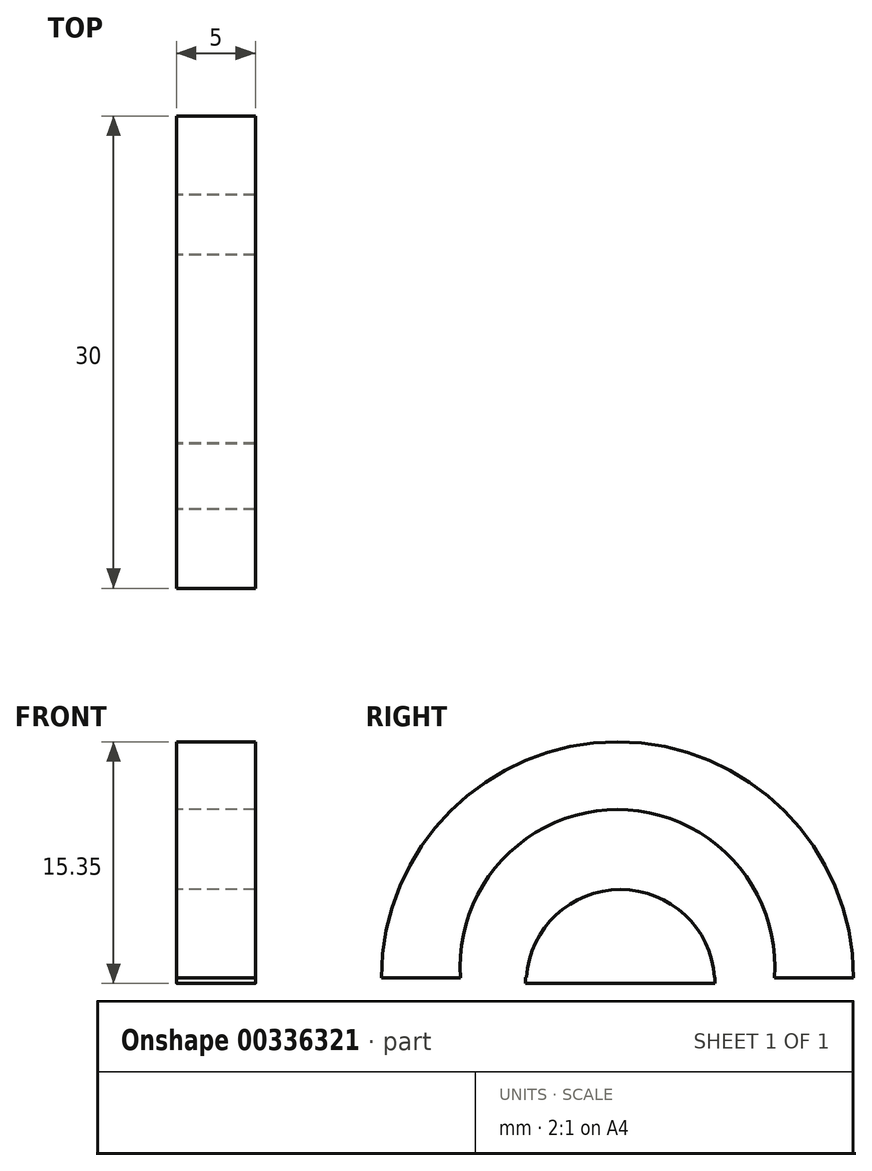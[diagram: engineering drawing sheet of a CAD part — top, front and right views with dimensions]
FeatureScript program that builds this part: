
annotation { "Feature Type Name" : "Feature", "Feature Type Description" : "" }
export const myFeature = defineFeature(function(context is Context, id is Id, definition is map)
    precondition{}
    {
        {
            var Q0;
            Q0=qCreatedBy(makeId("Right.planeOp"),FACE);
            var sketch = newSketch(context, id + "F0", { "sketchPlane" : qUnion([Q0])});
            skArc(sketch, "E0", {"start": v(-18.96, 22.33) * mm, "mid": v(-33.96, 37.33) * mm, "end": v(-48.96, 22.33) * mm});
            skLineSegment(sketch, "E1", {"start": v(-48.96, 22.33) * mm, "end": v(-18.96, 22.33) * mm});
            skArc(sketch, "E2", {"start": v(-26.16, 22.33) * mm, "mid": v(-33.96, 30.13) * mm, "end": v(-41.76, 22.33) * mm});
            skLineSegment(sketch, "E3", {"start": v(-41.76, 22.33) * mm, "end": v(-26.16, 22.33) * mm});
            skLineSegment(sketch, "E4", {"start": v(-33.96, 22.33) * mm, "end": v(-33.96, 30.13) * mm});
            skLineSegment(sketch, "E5", {"start": v(-33.96, 22.33) * mm, "end": v(-27.93, 27.27) * mm});
            skLineSegment(sketch, "E6", {"start": v(-33.96, 22.33) * mm, "end": v(-40.42, 26.7) * mm});
            skSolve(sketch);
        }
        {
            var Q0;
            {var subQ5=sQuery(id+"F0.wireOp",EDGE,"E0");Q0=makeQuery(id+"F0.imprint","IMPRINT",FACE,{"disambiguationData":[TD([[makeQuery(id+"F0.imprint","IMPRINT",EDGE,{"derivedFrom":subQ5}),1.0]])]});}
            var Q1;
            {var subQ3=sQuery(id+"F0.wireOp",EDGE,"E5");Q1=makeQuery(id+"F0.imprint","IMPRINT",FACE,{"disambiguationData":[TD([[makeQuery(id+"F0.imprint","IMPRINT",EDGE,{"derivedFrom":subQ3}),-1.0]])]});}
            var Q2;
            {var subQ0=sQuery(id+"F0.wireOp",EDGE,"E4");Q2=makeQuery(id+"F0.imprint","IMPRINT",FACE,{"disambiguationData":[TD([[makeQuery(id+"F0.imprint","IMPRINT",EDGE,{"derivedFrom":subQ0}),-1.0]])]});}
            var Q3;
            {var subQ0=sQuery(id+"F0.wireOp",EDGE,"E4");Q3=makeQuery(id+"F0.imprint","IMPRINT",FACE,{"disambiguationData":[TD([[makeQuery(id+"F0.imprint","IMPRINT",EDGE,{"derivedFrom":subQ0}),1.0]])]});}
            var Q4;
            {var subQ3=sQuery(id+"F0.wireOp",EDGE,"E6");Q4=makeQuery(id+"F0.imprint","IMPRINT",FACE,{"disambiguationData":[TD([[makeQuery(id+"F0.imprint","IMPRINT",EDGE,{"derivedFrom":subQ3}),1.0]])]});}
            extrude(context, id + "F1", {"entities" : qUnion([Q0, Q1, Q2, Q3, Q4]), "depth" : 5 * mm});
        }
        {
            var Q0;
            Q0=qCreatedBy(makeId("Right.planeOp"),FACE);
            var sketch = newSketch(context, id + "F2", { "sketchPlane" : qUnion([Q0])});
            skArc(sketch, "E7", {"start": v(-26.7, 22.29) * mm, "mid": v(-33.96, 30.33) * mm, "end": v(-41.22, 22.29) * mm});
            skLineSegment(sketch, "E8", {"start": v(-26.7, 22.29) * mm, "end": v(-41.22, 22.29) * mm});
            skArc(sketch, "E9", {"start": v(-30.31, 22.29) * mm, "mid": v(-33.96, 26.75) * mm, "end": v(-37.6, 22.29) * mm});
            skLineSegment(sketch, "E10", {"start": v(-30.31, 22.29) * mm, "end": v(-37.6, 22.29) * mm});
            skSolve(sketch);
        }
        {
            var Q0;
            Q0=sQuery(id+"F2.wireOp",VERTEX,"E9.center");
            var Q1;
            Q1=makeQuery(id+"F1.opExtrude","SWEPT_BODY",BODY,{"disambiguationData":[OSD([sQuery(id+"F0.wireOp",EDGE,"E0"),sQuery(id+"F0.wireOp",EDGE,"E1"),sQuery(id+"F0.wireOp",EDGE,"E3")])]});
            hole(context, id + "F3", {"style" : HoleStyle.SIMPLE, "endStyle" : HoleEndStyle.THROUGH, "oppositeDirection" : true, "holeDiameter" : 20 * mm, "tappedDepth" : 12 * mm, "tapClearance" : 3, "locations" : qUnion([Q0]), "scope" : qUnion([Q1])});
        }
        {
            var Q0;
            Q0=qCreatedBy(makeId("Right.planeOp"),FACE);
            var sketch = newSketch(context, id + "F4", { "sketchPlane" : qUnion([Q0])});
            skLineSegment(sketch, "E11", {"start": v(-18.77, 21.98) * mm, "end": v(-48.76, 21.98) * mm});
            skArc(sketch, "E12", {"start": v(-27.79, 21.98) * mm, "mid": v(-33.77, 27.96) * mm, "end": v(-39.75, 21.98) * mm});
            skLineSegment(sketch, "E13", {"start": v(-27.79, 21.98) * mm, "end": v(-39.75, 21.98) * mm});
            skSolve(sketch);
        }
        {
            var Q0;
            Q0 = qSketchRegion(id + "F4", true);
            extrude(context, id + "F5", {"entities" : qUnion([Q0]), "depth" : 5 * mm});
        }
        {
            var Q0;
            Q0=qCreatedBy(makeId("Right.planeOp"),FACE);
            var sketch = newSketch(context, id + "F6", { "sketchPlane" : qUnion([Q0])});
            skLineSegment(sketch, "E14", {"start": v(-19.04, 22.36) * mm, "end": v(-48.85, 22.36) * mm});
            skLineSegment(sketch, "E15", {"start": v(-27.78, 22) * mm, "end": v(-39.79, 22) * mm});
            skLineSegment(sketch, "E16", {"start": v(-39.79, 22) * mm, "end": v(-39.79, 22.36) * mm});
            skLineSegment(sketch, "E17", {"start": v(-39.79, 22.36) * mm, "end": v(-27.77, 22.36) * mm});
            skLineSegment(sketch, "E18", {"start": v(-27.77, 22.36) * mm, "end": v(-27.78, 22) * mm});
            skSolve(sketch);
        }
        {
            var Q0;
            Q0 = qSketchRegion(id + "F6", true);
            extrude(context, id + "F7", {"entities" : qUnion([Q0]), "operationType" : NewBodyOperationType.ADD, "depth" : 5 * mm});
        }
    });
